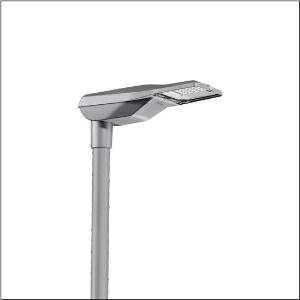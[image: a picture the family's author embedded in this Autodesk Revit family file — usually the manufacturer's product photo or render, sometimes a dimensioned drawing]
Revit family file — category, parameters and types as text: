
# Revit family: streetlight_sl_21_iq_micro___stw1_0a_5xe1e41g08cb_8385
name_source: partatom
category: Lighting Fixtures
units: mm (PartAtom-declared; Revit-internal decimal feet)

## family parameters
Cut with Voids When Loaded = No
Host = Face
Light Source = No
Part Type = Normal
Room Calculation Point = No
Round Connector Dimension = Use Diameter
Shared = No

## types (1)
- --- (1 x LED, 2980 lm, 19.4 W, 4000K)
    Apparent Load = 19 VA
    CIE Flux Codes = 38 75 98 100 100
    Color Rendering = 70
    Color Temperature = 4000K
    Default Elevation = 1800 mm
    Description = Streetlight SL 21 iQ micro, mast luminaire, primary light control with lens, of PMMA, primary optical cover: cover, of toughened safety glass, transparent, light distribution: STW1.0a, light emission: direct distribution, primary light characteristic: asymmetric, installation type: post-top, side-entry, LED, High Power LED, rated luminous flux: 2.980lm, luminous efficacy: 154lm/W, light colour: 740, colour temperature: 4000K, control: Street-Remote, Auto-Match, Temp-Guard, Lumen-Switch, Night-Set, Smart-Wire, Light-Fading, Desk-Remote (wireless, voltage-free reading and setting of iQ features in the workshop via application-optimized NFC function/RFID function), optimised constant luminous flux control (CLO 2.0), presetting dimming linear, mains connection: 220..240V, AC, 50/60Hz, start of lifetime: 19W, end of service life: 20W, reduction: 10W, luminaire housing, of diecast aluminium, powder-coated, Siteco® metallic grey (DB 702S), corrosivity category C5 mid according to DIN EN ISO 12944, please order mast flange separately, inclination adjustable: 0°, 5°, 10°, 15°, sealing non-destructively replaceable, multi-level sealing system, length: 528mm, width: 235mm, height: 110mm, mast flange for spigot size: 42mm (side-entry): 5XC10008XM4, 60/48mm (side-entry/post-top): 5XC10108XM2, 76/60mm (side-entry/post-top): 5XC10108XM1, protection rating (complete): IP66, insulation class (complete): insulation class II (safety insulation), certification: CE, ENEC, ENEC+, VDE, impact resistance: IK09, permissible operating ambient temperature for outdoor applications: -40..+50°C, standard-compliant lighting for roads and squares, packaging unit: 1 piece

Light Distribution: STW1.0a
    Height = 110 mm
    Lamp = 1 x LED
    Lamp Light Flux = 2980 lm
    Lamp Power = 19.4 W
    Lamp count = 1
    Length = 528 mm
    Luminous efficacy = 154 lm/W
    Manufacturer = Siteco
    ModVariant = No
    Model = 5XE1E41G08CB
    Number of Poles = 1
    OnlyDefault = Yes
    Power Factor = 1
    Product Name = Streetlight SL 21 iQ micro | STW1.0a
    Product group = mast luminaire | pylon top
    ProductGroupID = 6100
    Protection Class = Protection class II
    Protection Degree = IP 66
    RLX_Detail_Level = 1
    RLX_Emergency_Light_Flux = 0 lm
    RLX_Emergency_Type = 0
    RLX_Emergency_Type_DB = No
    RlxData = <blob elided: 98645 chars, md5=4afccf8d>
    Socket = socket
    Standby Power = 0 W
    System Light Flux = 2980 lm
    System Power = 19 W
    Type Comments = factory setting: luminous flux: 100 % | dim-lin: 254 | 387 mA
    Type Image = l_1006881.jpg
    URL = http://relux.com
    VarID = @adj_088157
    Voltage = 0 V
    Weight = 0.00 kg
    Width = 235 mm

## geometry (parser evidence)
native form markers: Blend x4, Sweep x10
no freeform markers — native parametric forms only
